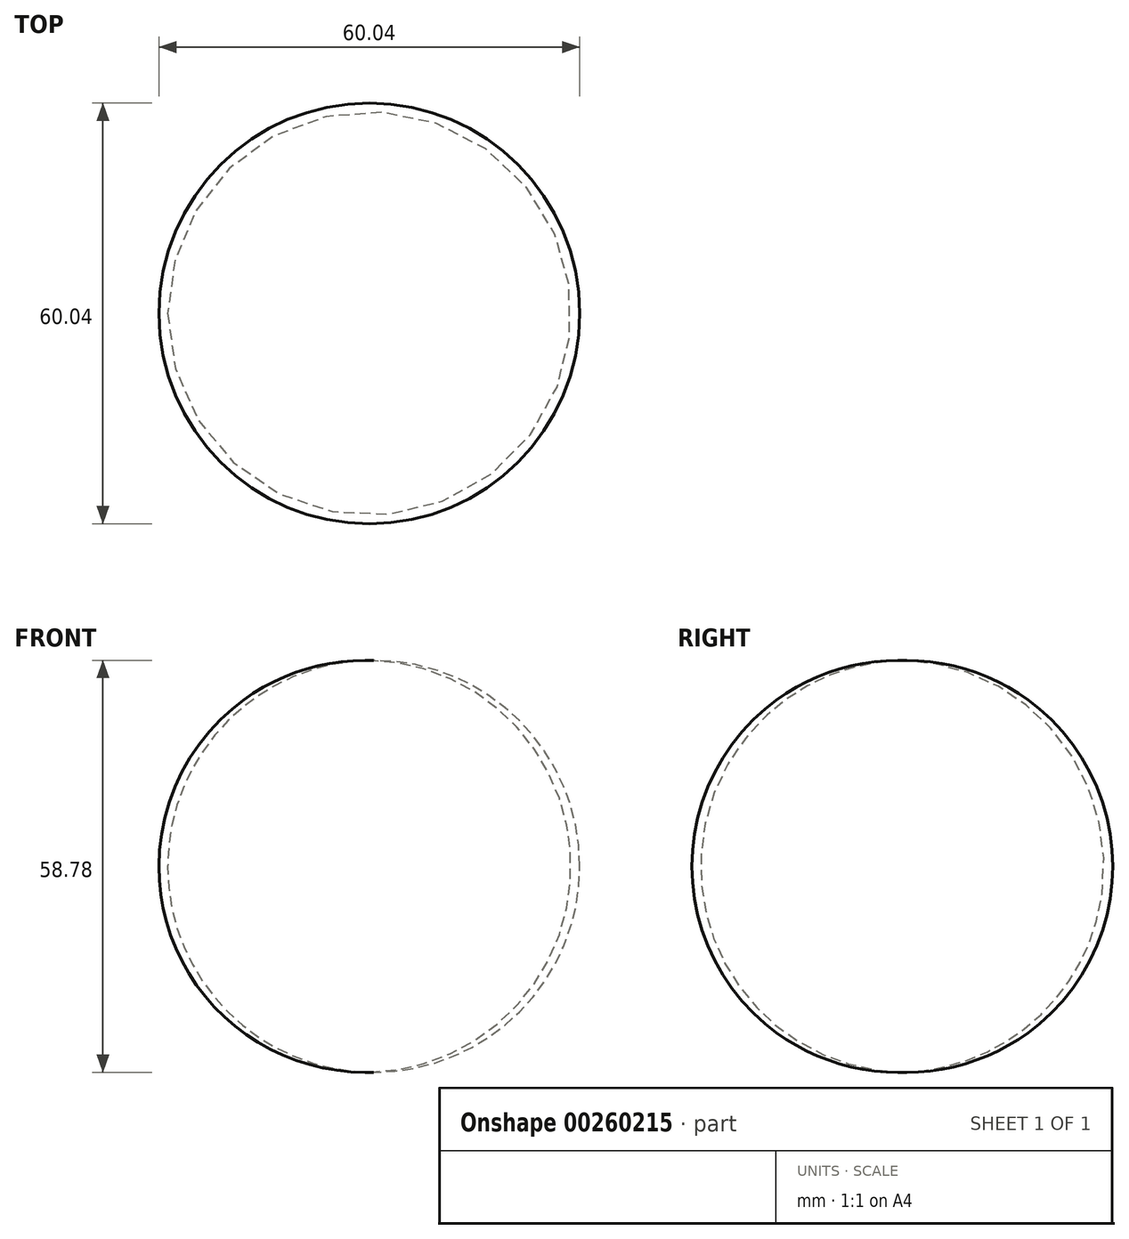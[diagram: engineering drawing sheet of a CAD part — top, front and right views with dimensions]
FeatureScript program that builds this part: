
annotation { "Feature Type Name" : "Feature", "Feature Type Description" : "" }
export const myFeature = defineFeature(function(context is Context, id is Id, definition is map)
    precondition{}
    {
        {
            var Q0;
            Q0=qCreatedBy(makeId("Front.planeOp"),FACE);
            var sketch = newSketch(context, id + "F0", { "sketchPlane" : qUnion([Q0])});
            skArc(sketch, "E0", {"start": v(0, 29.39) * mm, "mid": v(-30.02, 0) * mm, "end": v(0, -29.39) * mm});
            skLineSegment(sketch, "E1", {"start": v(0, 75.94) * mm, "end": v(0, -73.03) * mm, "construction": true});
            skLineSegment(sketch, "E2", {"start": v(0, 29.39) * mm, "end": v(0, -29.39) * mm});
            skSolve(sketch);
        }
        {
            var Q0;
            Q0=makeQuery(id+"F0.imprint","IMPRINT",FACE,{"disambiguationData":[TD([[makeQuery(id+"F0.imprint","IMPRINT",EDGE,{"derivedFrom":sQuery(id+"F0.wireOp",EDGE,"E0")}),1.0]])]});
            var Q1;
            Q1=sQuery(id+"F0.wireOp",EDGE,"E1");
            revolve(context, id + "F1", {"entities" : qUnion([Q0]), "axis" : qUnion([Q1]), "revolveType" : RevolveType.FULL});
        }
    });
